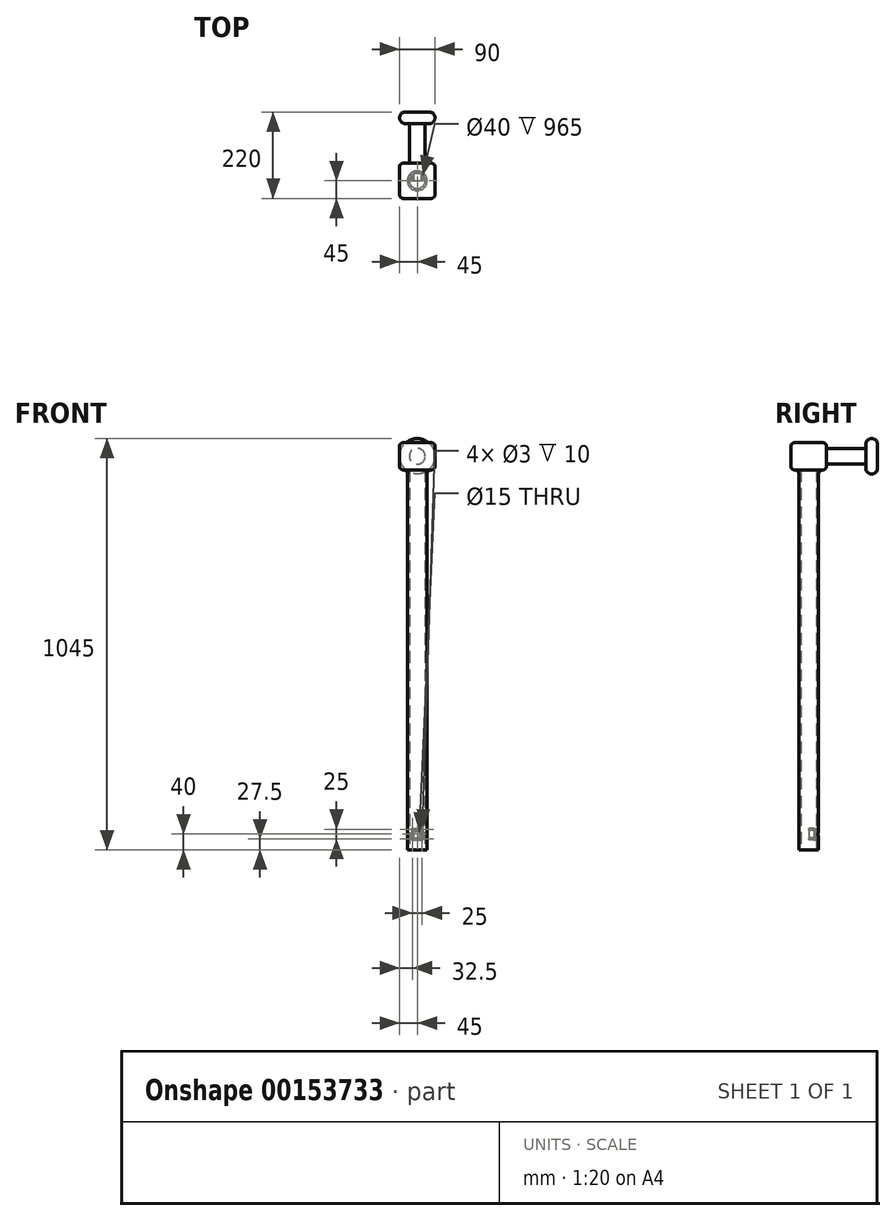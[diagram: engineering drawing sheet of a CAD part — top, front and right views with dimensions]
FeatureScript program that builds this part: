
annotation { "Feature Type Name" : "Feature", "Feature Type Description" : "" }
export const myFeature = defineFeature(function(context is Context, id is Id, definition is map)
    precondition{}
    {
        {
            var Q0;
            Q0=qCreatedBy(makeId("Top.planeOp"),FACE);
            var sketch = newSketch(context, id + "F0", { "sketchPlane" : qUnion([Q0])});
            skCircle(sketch, "E0", {"center": v(0, 0) * mm, "radius": 25 * mm});
            skCircle(sketch, "E1", {"center": v(0, 0) * mm, "radius": 20 * mm});
            skSolve(sketch);
        }
        {
            var Q0;
            Q0 = qSketchRegion(id + "F0", true);
            extrude(context, id + "F1", {"entities" : qUnion([Q0]), "depth" : 1000 * mm});
        }
        {
            var Q0;
            Q0=qCreatedBy(makeId("Front.planeOp"),FACE);
            var sketch = newSketch(context, id + "F2", { "sketchPlane" : qUnion([Q0])});
            skCircle(sketch, "E2", {"center": v(0, 40) * mm, "radius": 7.5 * mm});
            skSolve(sketch);
        }
        {
            var Q0;
            Q0 = qSketchRegion(id + "F2", true);
            extrude(context, id + "F3", {"entities" : qUnion([Q0]), "operationType" : NewBodyOperationType.REMOVE, "oppositeDirection" : true, "depth" : 25 * mm});
        }
        {
            var Q0;
            Q0=qCreatedBy(makeId("Front.planeOp"),FACE);
            var sketch = newSketch(context, id + "F4", { "sketchPlane" : qUnion([Q0])});
            skLineSegment(sketch, "E3.bottom", {"start": v(-10, 50) * mm, "end": v(10, 50) * mm});
            skLineSegment(sketch, "E3.top", {"start": v(-10, 30) * mm, "end": v(10, 30) * mm});
            skLineSegment(sketch, "E3.left", {"start": v(-10, 50) * mm, "end": v(-10, 30) * mm});
            skLineSegment(sketch, "E3.right", {"start": v(10, 50) * mm, "end": v(10, 30) * mm});
            skCircle(sketch, "E4.0", {"center": v(0, 40) * mm, "radius": 7.5 * mm, "construction": true});
            skPoint(sketch, "E5", {"position": v(-10, 40) * mm});
            skPoint(sketch, "E6", {"position": v(0, 30) * mm});
            skLineSegment(sketch, "E7.0", {"start": v(-15, 25) * mm, "end": v(15, 25) * mm});
            skLineSegment(sketch, "E7.1", {"start": v(-15, 55) * mm, "end": v(-15, 25) * mm});
            skLineSegment(sketch, "E7.2", {"start": v(-15, 55) * mm, "end": v(15, 55) * mm});
            skLineSegment(sketch, "E7.3", {"start": v(15, 55) * mm, "end": v(15, 25) * mm});
            skSolve(sketch);
        }
        {
            var Q0;
            Q0 = qSketchRegion(id + "F4", true);
            extrude(context, id + "F5", {"entities" : qUnion([Q0]), "operationType" : NewBodyOperationType.ADD, "endBound" : BoundingType.UP_TO_NEXT, "oppositeDirection" : true, "depth" : 25 * mm});
        }
        {
            var Q0;
            Q0=makeQuery(id+"F5.opExtrude","CAP_FACE",FACE,{"disambiguationData":[OSD([sQuery(id+"F4.wireOp",EDGE,"E3.bottom"),sQuery(id+"F4.wireOp",EDGE,"E3.top"),sQuery(id+"F4.wireOp",EDGE,"E3.left"),sQuery(id+"F4.wireOp",EDGE,"E3.right"),sQuery(id+"F4.wireOp",EDGE,"E7.0"),sQuery(id+"F4.wireOp",EDGE,"E7.1"),sQuery(id+"F4.wireOp",EDGE,"E7.2"),sQuery(id+"F4.wireOp",EDGE,"E7.3")])],"isStart":true});
            var sketch = newSketch(context, id + "F6", { "sketchPlane" : qUnion([Q0])});
            skCircle(sketch, "E8", {"center": v(-12.5, 52.5) * mm, "radius": 1.5 * mm});
            skLineSegment(sketch, "E9.bottom", {"start": v(-10, 50) * mm, "end": v(-15, 50) * mm, "construction": true});
            skLineSegment(sketch, "E9.top", {"start": v(-10, 55) * mm, "end": v(-15, 55) * mm, "construction": true});
            skLineSegment(sketch, "E9.left", {"start": v(-10, 50) * mm, "end": v(-10, 55) * mm, "construction": true});
            skLineSegment(sketch, "E9.right", {"start": v(-15, 50) * mm, "end": v(-15, 55) * mm, "construction": true});
            skPoint(sketch, "E10", {"position": v(-15, 52.5) * mm});
            skPoint(sketch, "E11", {"position": v(-12.5, 50) * mm});
            skLineSegment(sketch, "E12", {"start": v(0, 25) * mm, "end": v(0, 69) * mm, "construction": true});
            skPoint(sketch, "E12.endSnap0", {"position": v(0, 55) * mm});
            skLineSegment(sketch, "E13", {"start": v(-15, 40) * mm, "end": v(15, 40) * mm, "construction": true});
            skCircle(sketch, "E14.MirrorC", {"center": v(12.5, 52.5) * mm, "radius": 1.5 * mm});
            skCircle(sketch, "E15.MirrorC", {"center": v(12.5, 27.5) * mm, "radius": 1.5 * mm});
            skCircle(sketch, "E16.MirrorC", {"center": v(-12.5, 27.5) * mm, "radius": 1.5 * mm});
            skSolve(sketch);
        }
        {
            var Q0;
            Q0 = qSketchRegion(id + "F6", true);
            extrude(context, id + "F7", {"entities" : qUnion([Q0]), "operationType" : NewBodyOperationType.REMOVE, "oppositeDirection" : true, "depth" : 10 * mm});
        }
        {
            var Q0;
            Q0=qCreatedBy(makeId("Right.planeOp"),FACE);
            var sketch = newSketch(context, id + "F8", { "sketchPlane" : qUnion([Q0])});
            skLineSegment(sketch, "E17.bottom", {"start": v(45, 965) * mm, "end": v(-45, 965) * mm});
            skLineSegment(sketch, "E17.top", {"start": v(45, 1035) * mm, "end": v(-45, 1035) * mm});
            skLineSegment(sketch, "E17.left", {"start": v(45, 965) * mm, "end": v(45, 1035) * mm});
            skLineSegment(sketch, "E17.right", {"start": v(-45, 965) * mm, "end": v(-45, 1035) * mm});
            skLineSegment(sketch, "E18", {"start": v(0, 293) * mm, "end": v(0, 1429.99) * mm, "construction": true});
            skPoint(sketch, "E19", {"position": v(0, 1035) * mm});
            skSolve(sketch);
        }
        {
            var Q0;
            Q0 = qSketchRegion(id + "F8", true);
            extrude(context, id + "F9", {"entities" : qUnion([Q0]), "operationType" : NewBodyOperationType.ADD, "depth" : 45 * mm, "hasSecondDirection" : true, "secondDirectionOppositeDirection" : true, "secondDirectionDepth" : 45 * mm});
        }
        {
            var Q0;
            Q0=makeQuery(id+"F9.opExtrude","SWEPT_FACE",FACE,{"disambiguationData":[OSD([sQuery(id+"F8.wireOp",EDGE,"E17.left")])]});
            var sketch = newSketch(context, id + "F10", { "sketchPlane" : qUnion([Q0])});
            skSolve(sketch);
        }
        {
            var Q0;
            {var subQ0=sQuery(id+"F8.wireOp",EDGE,"E17.left");Q0=makeQuery(id+"F10.imprint","IMPRINT",FACE,{"disambiguationData":[TD([[makeQuery(id+"F10.imprint","IMPRINT",EDGE,{"derivedFrom":makeQuery(id+"F9.opExtrude","CAP_EDGE",EDGE,{"disambiguationData":[OSD([subQ0])],"isStart":true})}),1.0]])]});}
            var sketch = newSketch(context, id + "F11", { "sketchPlane" : qUnion([Q0])});
            skCircle(sketch, "E20", {"center": v(0, 1000) * mm, "radius": 20 * mm});
            skLineSegment(sketch, "E21.0", {"start": v(-45, 965) * mm, "end": v(-45, 1035) * mm, "construction": true});
            skLineSegment(sketch, "E21.1", {"start": v(-45, 1035) * mm, "end": v(45, 1035) * mm, "construction": true});
            skPoint(sketch, "E22", {"position": v(-45, 1000) * mm});
            skPoint(sketch, "E23", {"position": v(0, 1035) * mm});
            skSolve(sketch);
        }
        {
            var Q0;
            Q0 = qSketchRegion(id + "F11", true);
            extrude(context, id + "F12", {"entities" : qUnion([Q0]), "operationType" : NewBodyOperationType.ADD, "depth" : 100 * mm});
        }
        {
            var Q0;
            Q0=makeQuery(id+"F12.opExtrude","CAP_FACE",FACE,{"disambiguationData":[OSD([sQuery(id+"F11.wireOp",EDGE,"E20")])],"isStart":false});
            var sketch = newSketch(context, id + "F13", { "sketchPlane" : qUnion([Q0])});
            skCircle(sketch, "E24", {"center": v(0, 1000) * mm, "radius": 45 * mm});
            skSolve(sketch);
        }
        {
            var Q0;
            Q0 = qSketchRegion(id + "F13", true);
            extrude(context, id + "F14", {"entities" : qUnion([Q0]), "operationType" : NewBodyOperationType.ADD, "depth" : 30 * mm});
        }
        {
            var Q0;
            Q0=makeQuery(id+"F14.opExtrude","CAP_EDGE",EDGE,{"disambiguationData":[OSD([sQuery(id+"F13.wireOp",EDGE,"E24")])],"isStart":false});
            var Q1;
            Q1=makeQuery(id+"F14.opExtrude","CAP_EDGE",EDGE,{"disambiguationData":[OSD([sQuery(id+"F13.wireOp",EDGE,"E24")])],"isStart":true});
            var Q2;
            Q2=makeQuery(id+"F12.opExtrude","CAP_EDGE",EDGE,{"disambiguationData":[OSD([sQuery(id+"F11.wireOp",EDGE,"E20")])],"isStart":true});
            fillet(context, id + "F15", {"entities" : qUnion([Q0, Q1, Q2]), "radius" : 15 * mm, "tangentPropagation" : true, "allowEdgeOverflow" : false});
        }
        {
            var Q0;
            Q0=makeQuery(id+"F9.opExtrude","CAP_FACE",FACE,{"disambiguationData":[OSD([sQuery(id+"F8.wireOp",EDGE,"E17.bottom"),sQuery(id+"F8.wireOp",EDGE,"E17.top"),sQuery(id+"F8.wireOp",EDGE,"E17.left"),sQuery(id+"F8.wireOp",EDGE,"E17.right")])],"isStart":true});
            var Q1;
            {var subQ3=sQuery(id+"F8.wireOp",EDGE,"E17.bottom");Q1=makeQuery(id+"F9.boolean.opBoolean","SPLIT",FACE,{"disambiguationData":[TD([makeQuery(id+"F1.opExtrude","SWEPT_FACE",FACE,{"disambiguationData":[OSD([sQuery(id+"F0.wireOp",EDGE,"E0")])]})])],"derivedFrom":makeQuery(id+"F9.opExtrude","SWEPT_FACE",FACE,{"disambiguationData":[OSD([subQ3])]})});}
            var Q2;
            Q2=makeQuery(id+"F9.opExtrude","SWEPT_FACE",FACE,{"disambiguationData":[OSD([sQuery(id+"F8.wireOp",EDGE,"E17.top")])]});
            var Q3;
            Q3=makeQuery(id+"F9.opExtrude","CAP_FACE",FACE,{"disambiguationData":[OSD([sQuery(id+"F8.wireOp",EDGE,"E17.bottom"),sQuery(id+"F8.wireOp",EDGE,"E17.top"),sQuery(id+"F8.wireOp",EDGE,"E17.left"),sQuery(id+"F8.wireOp",EDGE,"E17.right")])],"isStart":false});
            fillet(context, id + "F16", {"entities" : qUnion([Q0, Q1, Q2, Q3]), "radius" : 10 * mm, "tangentPropagation" : true, "allowEdgeOverflow" : false});
        }
    });
